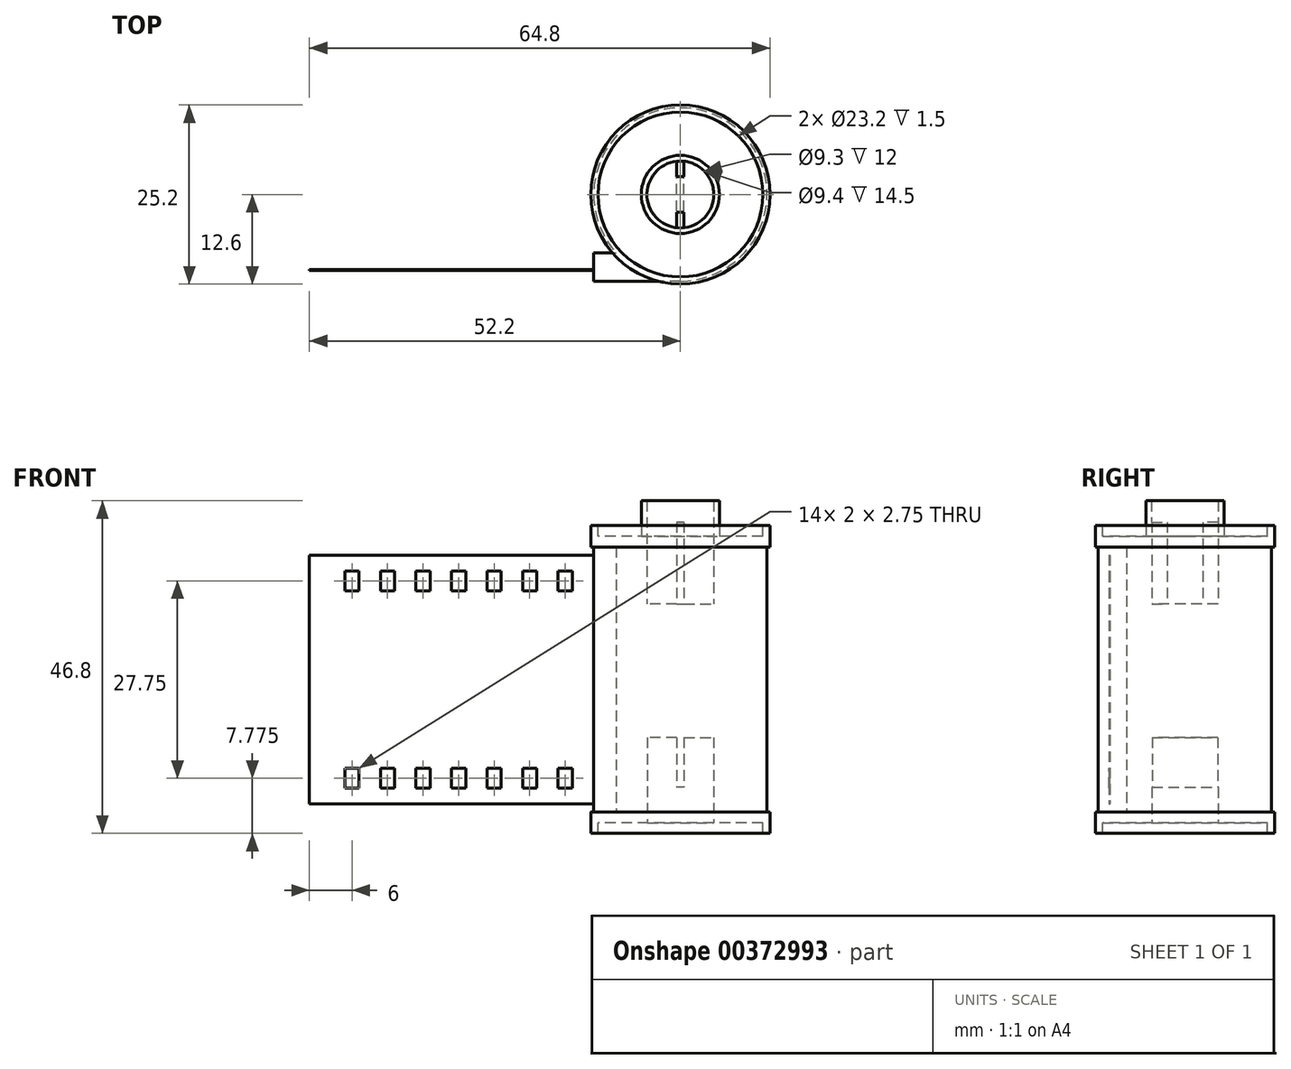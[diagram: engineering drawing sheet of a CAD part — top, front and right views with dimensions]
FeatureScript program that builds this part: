
annotation { "Feature Type Name" : "Feature", "Feature Type Description" : "" }
export const myFeature = defineFeature(function(context is Context, id is Id, definition is map)
    precondition{}
    {
        {
            var Q0;
            Q0=qCreatedBy(makeId("Top.planeOp"),FACE);
            var sketch = newSketch(context, id + "F0", { "sketchPlane" : qUnion([Q0])});
            skArc(sketch, "E0", {"start": v(0, -12.2) * mm, "mid": v(4.94, 11.16) * mm, "end": v(-9.03, -8.2) * mm});
            skLineSegment(sketch, "E1", {"start": v(0, -12.2) * mm, "end": v(-12.2, -12.2) * mm});
            skLineSegment(sketch, "E2", {"start": v(-12.2, -12.2) * mm, "end": v(-12.2, -8.2) * mm});
            skLineSegment(sketch, "E3", {"start": v(-12.2, -8.2) * mm, "end": v(-9.03, -8.2) * mm});
            skLineSegment(sketch, "E4", {"start": v(-12.2, -8.2) * mm, "end": v(-12.2, 0) * mm, "construction": true});
            skSolve(sketch);
        }
        {
            var Q0;
            Q0=makeQuery(id+"F0.imprint","IMPRINT",FACE,{"disambiguationData":[TD([[makeQuery(id+"F0.imprint","IMPRINT",EDGE,{"derivedFrom":sQuery(id+"F0.wireOp",EDGE,"E0")}),1.0]])]});
            extrude(context, id + "F1", {"entities" : qUnion([Q0]), "depth" : 37.3 * mm, "symmetric" : true});
        }
        {
            var Q0;
            Q0=qCreatedBy(makeId("Front.planeOp"),FACE);
            var sketch = newSketch(context, id + "F2", { "sketchPlane" : qUnion([Q0])});
            skLineSegment(sketch, "E5", {"start": v(0, -18.65) * mm, "end": v(12.6, -18.65) * mm});
            skLineSegment(sketch, "E6", {"start": v(12.6, -18.65) * mm, "end": v(12.6, -21.65) * mm});
            skLineSegment(sketch, "E7", {"start": v(11.6, -21.65) * mm, "end": v(11.6, -20.15) * mm});
            skLineSegment(sketch, "E8", {"start": v(11.6, -20.15) * mm, "end": v(0, -20.15) * mm});
            skLineSegment(sketch, "E9", {"start": v(11.6, -21.65) * mm, "end": v(12.6, -21.65) * mm});
            skLineSegment(sketch, "E10", {"start": v(0, -18.65) * mm, "end": v(0, -20.15) * mm});
            skSolve(sketch);
        }
        {
            var Q0;
            Q0=makeQuery(id+"F2.imprint","IMPRINT",FACE,{"disambiguationData":[TD([[makeQuery(id+"F2.imprint","IMPRINT",EDGE,{"derivedFrom":sQuery(id+"F2.wireOp",EDGE,"E5")}),-1.0]])]});
            var Q1;
            Q1=sQuery(id+"F2.wireOp",EDGE,"E10");
            revolve(context, id + "F3", {"operationType" : NewBodyOperationType.ADD, "entities" : qUnion([Q0]), "axis" : qUnion([Q1]), "revolveType" : RevolveType.FULL});
        }
        {
            var Q0;
            Q0=makeQuery(id+"F3.opRevolve","SWEPT_FACE",FACE,{"disambiguationData":[OSD([sQuery(id+"F2.wireOp",EDGE,"E8")])]});
            var sketch = newSketch(context, id + "F4", { "sketchPlane" : qUnion([Q0])});
            skCircle(sketch, "E11", {"center": v(0, 0) * mm, "radius": 4.65 * mm});
            skSolve(sketch);
        }
        {
            var Q0;
            Q0=makeQuery(id+"F4.imprint","IMPRINT",FACE,{"disambiguationData":[TD([[makeQuery(id+"F4.imprint","IMPRINT",EDGE,{"derivedFrom":sQuery(id+"F4.wireOp",EDGE,"E11")}),1.0]])]});
            extrude(context, id + "F5", {"entities" : qUnion([Q0]), "operationType" : NewBodyOperationType.REMOVE, "oppositeDirection" : true, "depth" : 5 * mm});
        }
        {
            var Q0;
            Q0=makeQuery(id+"F5.boolean.opBoolean","COPY",FACE,{"derivedFrom":makeQuery(id+"F5.opExtrude","CAP_FACE",FACE,{"disambiguationData":[OSD([sQuery(id+"F4.wireOp",EDGE,"E11")])],"isStart":false})});
            var sketch = newSketch(context, id + "F6", { "sketchPlane" : qUnion([Q0])});
            skArc(sketch, "E12", {"start": v(-0.5, 4.62) * mm, "mid": v(-4.65, 0) * mm, "end": v(-0.5, -4.62) * mm});
            skLineSegment(sketch, "E13", {"start": v(-0.5, 4.62) * mm, "end": v(-0.5, -4.62) * mm});
            skLineSegment(sketch, "E14", {"start": v(0, 0) * mm, "end": v(0, -10.24) * mm, "construction": true});
            skLineSegment(sketch, "E15.MirrorCS", {"start": v(0.5, 4.62) * mm, "end": v(0.5, -4.62) * mm});
            skArc(sketch, "E16.trimOffspring", {"start": v(0.5, -4.62) * mm, "mid": v(4.65, 0) * mm, "end": v(0.5, 4.62) * mm});
            skSolve(sketch);
        }
        {
            var Q0;
            Q0=makeQuery(id+"F6.imprint","IMPRINT",FACE,{"disambiguationData":[TD([[makeQuery(id+"F6.imprint","IMPRINT",EDGE,{"derivedFrom":sQuery(id+"F6.wireOp",EDGE,"E12")}),1.0]])]});
            var Q1;
            Q1=makeQuery(id+"F6.imprint","IMPRINT",FACE,{"disambiguationData":[TD([[makeQuery(id+"F6.imprint","IMPRINT",EDGE,{"derivedFrom":sQuery(id+"F6.wireOp",EDGE,"E15.MirrorCS")}),1.0]])]});
            extrude(context, id + "F7", {"entities" : qUnion([Q0, Q1]), "operationType" : NewBodyOperationType.REMOVE, "oppositeDirection" : true, "depth" : 7 * mm});
        }
        {
            var Q0;
            Q0=qCreatedBy(makeId("Front.planeOp"),FACE);
            var sketch = newSketch(context, id + "F8", { "sketchPlane" : qUnion([Q0])});
            skLineSegment(sketch, "E17", {"start": v(0, 18.65) * mm, "end": v(12.6, 18.65) * mm});
            skLineSegment(sketch, "E18", {"start": v(12.6, 18.65) * mm, "end": v(12.6, 21.65) * mm});
            skLineSegment(sketch, "E19", {"start": v(12.6, 21.65) * mm, "end": v(11.6, 21.65) * mm});
            skLineSegment(sketch, "E20", {"start": v(11.6, 21.65) * mm, "end": v(11.6, 20.15) * mm});
            skLineSegment(sketch, "E21", {"start": v(11.6, 20.15) * mm, "end": v(0, 20.15) * mm});
            skLineSegment(sketch, "E22", {"start": v(0, 20.15) * mm, "end": v(0, 18.65) * mm});
            skSolve(sketch);
        }
        {
            var Q0;
            Q0 = qSketchRegion(id + "F8", true);
            var Q1;
            Q1=sQuery(id+"F8.wireOp",EDGE,"E22");
            revolve(context, id + "F9", {"operationType" : NewBodyOperationType.ADD, "entities" : qUnion([Q0]), "axis" : qUnion([Q1]), "revolveType" : RevolveType.FULL});
        }
        {
            var Q0;
            Q0=makeQuery(id+"F9.opRevolve","SWEPT_FACE",FACE,{"disambiguationData":[OSD([sQuery(id+"F8.wireOp",EDGE,"E21")])]});
            var sketch = newSketch(context, id + "F10", { "sketchPlane" : qUnion([Q0])});
            skCircle(sketch, "E23", {"center": v(0, 0) * mm, "radius": 5.5 * mm});
            skCircle(sketch, "E24", {"center": v(0, 0) * mm, "radius": 4.7 * mm});
            skSolve(sketch);
        }
        {
            var Q0;
            Q0 = qSketchRegion(id + "F10", true);
            extrude(context, id + "F11", {"entities" : qUnion([Q0]), "operationType" : NewBodyOperationType.ADD, "depth" : 5 * mm});
        }
        {
            var Q0;
            Q0=makeQuery(id+"F11.boolean.opBoolean","SPLIT",FACE,{"disambiguationData":[TD([makeQuery(id+"F11.opExtrude","SWEPT_FACE",FACE,{"disambiguationData":[OSD([sQuery(id+"F10.wireOp",EDGE,"E24")])]})])],"derivedFrom":makeQuery(id+"F9.opRevolve","SWEPT_FACE",FACE,{"disambiguationData":[OSD([sQuery(id+"F8.wireOp",EDGE,"E21")])]})});
            var sketch = newSketch(context, id + "F12", { "sketchPlane" : qUnion([Q0])});
            skCircle(sketch, "E25.0", {"center": v(0, 0) * mm, "radius": 4.7 * mm});
            skSolve(sketch);
        }
        {
            var Q0;
            Q0=makeQuery(id+"F12.imprint","IMPRINT",FACE,{"disambiguationData":[TD([[makeQuery(id+"F12.imprint","IMPRINT",EDGE,{"derivedFrom":sQuery(id+"F12.wireOp",EDGE,"E25.0")}),1.0]])]});
            var Q1;
            Q1=sQuery(id+"F12.wireOp",EDGE,"E25.0");
            extrude(context, id + "F13", {"entities" : qUnion([Q0]), "operationType" : NewBodyOperationType.REMOVE, "surfaceEntities" : qUnion([Q1]), "oppositeDirection" : true, "depth" : 9.5 * mm});
        }
        {
            var Q0;
            Q0=makeQuery(id+"F13.boolean.opBoolean","COPY",FACE,{"derivedFrom":makeQuery(id+"F13.opExtrude","CAP_FACE",FACE,{"disambiguationData":[OSD([sQuery(id+"F12.wireOp",EDGE,"E25.0")])],"isStart":false})});
            var sketch = newSketch(context, id + "F14", { "sketchPlane" : qUnion([Q0])});
            skLineSegment(sketch, "E26", {"start": v(0, 0) * mm, "end": v(0, 19.86) * mm, "construction": true});
            skLineSegment(sketch, "E27", {"start": v(-0.5, 4.67) * mm, "end": v(-0.5, 2.5) * mm});
            skLineSegment(sketch, "E28.MirrorCS", {"start": v(0.5, 4.67) * mm, "end": v(0.5, 2.5) * mm});
            skLineSegment(sketch, "E29", {"start": v(-0.5, 2.5) * mm, "end": v(0.5, 2.5) * mm});
            skLineSegment(sketch, "E30", {"start": v(0, 0) * mm, "end": v(21.48, 0) * mm, "construction": true});
            skPoint(sketch, "E31.orphan", {"position": v(0.5, 8.35) * mm});
            skPoint(sketch, "E32.orphan", {"position": v(-0.5, 8.35) * mm});
            skLineSegment(sketch, "E33.MirrorCS", {"start": v(0.5, -4.67) * mm, "end": v(0.5, -2.5) * mm});
            skLineSegment(sketch, "E34.MirrorCS", {"start": v(-0.5, -2.5) * mm, "end": v(0.5, -2.5) * mm});
            skLineSegment(sketch, "E35.MirrorCS", {"start": v(-0.5, -4.67) * mm, "end": v(-0.5, -2.5) * mm});
            skArc(sketch, "E36.converted", {"start": v(-0.5, -4.67) * mm, "mid": v(3.14, -3.5) * mm, "end": v(4.7, 0) * mm});
            skArc(sketch, "E37.trimOffspring", {"start": v(0.5, 4.67) * mm, "mid": v(0, 4.7) * mm, "end": v(-0.5, 4.67) * mm});
            skSolve(sketch);
        }
        {
            var Q0;
            Q0 = qSketchRegion(id + "F14", true);
            extrude(context, id + "F15", {"entities" : qUnion([Q0]), "operationType" : NewBodyOperationType.ADD, "depth" : 11.5 * mm});
        }
        {
            var Q0;
            Q0=makeQuery(id+"F1.opExtrude","SWEPT_FACE",FACE,{"disambiguationData":[OSD([sQuery(id+"F0.wireOp",EDGE,"E1")])]});
            cPlane(context, id + "F16", {"entities" : qUnion([Q0]), "cplaneType" : CPlaneType.OFFSET, "offset" : 1.65 * mm, "oppositeDirection" : true, "width" : 150 * mm, "height" : 150 * mm});
        }
        {
            var Q0;
            Q0=qCreatedBy(id+"F16.planeOp",FACE);
            var sketch = newSketch(context, id + "F17", { "sketchPlane" : qUnion([Q0])});
            skLineSegment(sketch, "E38.bottom", {"start": v(-12.2, 17.5) * mm, "end": v(-52.2, 17.5) * mm});
            skLineSegment(sketch, "E38.top", {"start": v(-12.2, -17.5) * mm, "end": v(-52.2, -17.5) * mm});
            skLineSegment(sketch, "E38.left", {"start": v(-12.2, 17.5) * mm, "end": v(-12.2, -17.5) * mm});
            skLineSegment(sketch, "E38.right", {"start": v(-52.2, 17.5) * mm, "end": v(-52.2, -17.5) * mm});
            skLineSegment(sketch, "E39", {"start": v(-12.2, 0) * mm, "end": v(0, 0) * mm, "construction": true});
            skLineSegment(sketch, "E40.bottom", {"start": v(-15.2, 15.25) * mm, "end": v(-17.2, 15.25) * mm});
            skLineSegment(sketch, "E40.top", {"start": v(-15.2, 12.5) * mm, "end": v(-17.2, 12.5) * mm});
            skLineSegment(sketch, "E40.left", {"start": v(-15.2, 15.25) * mm, "end": v(-15.2, 12.5) * mm});
            skLineSegment(sketch, "E40.right", {"start": v(-17.2, 15.25) * mm, "end": v(-17.2, 12.5) * mm});
            skLineSegment(sketch, "E41.1.0.0", {"start": v(-20.2, 15.25) * mm, "end": v(-22.2, 15.25) * mm});
            skLineSegment(sketch, "E41.1.0.1", {"start": v(-20.2, 12.5) * mm, "end": v(-22.2, 12.5) * mm});
            skLineSegment(sketch, "E41.1.0.2", {"start": v(-20.2, 15.25) * mm, "end": v(-20.2, 12.5) * mm});
            skLineSegment(sketch, "E41.1.0.3", {"start": v(-22.2, 15.25) * mm, "end": v(-22.2, 12.5) * mm});
            skLineSegment(sketch, "E41.2.0.0", {"start": v(-25.2, 15.25) * mm, "end": v(-27.2, 15.25) * mm});
            skLineSegment(sketch, "E41.2.0.1", {"start": v(-25.2, 12.5) * mm, "end": v(-27.2, 12.5) * mm});
            skLineSegment(sketch, "E41.2.0.2", {"start": v(-25.2, 15.25) * mm, "end": v(-25.2, 12.5) * mm});
            skLineSegment(sketch, "E41.2.0.3", {"start": v(-27.2, 15.25) * mm, "end": v(-27.2, 12.5) * mm});
            skLineSegment(sketch, "E41.3.0.0", {"start": v(-30.2, 15.25) * mm, "end": v(-32.2, 15.25) * mm});
            skLineSegment(sketch, "E41.3.0.1", {"start": v(-30.2, 12.5) * mm, "end": v(-32.2, 12.5) * mm});
            skLineSegment(sketch, "E41.3.0.2", {"start": v(-30.2, 15.25) * mm, "end": v(-30.2, 12.5) * mm});
            skLineSegment(sketch, "E41.3.0.3", {"start": v(-32.2, 15.25) * mm, "end": v(-32.2, 12.5) * mm});
            skLineSegment(sketch, "E41.4.0.0", {"start": v(-35.2, 15.25) * mm, "end": v(-37.2, 15.25) * mm});
            skLineSegment(sketch, "E41.4.0.1", {"start": v(-35.2, 12.5) * mm, "end": v(-37.2, 12.5) * mm});
            skLineSegment(sketch, "E41.4.0.2", {"start": v(-35.2, 15.25) * mm, "end": v(-35.2, 12.5) * mm});
            skLineSegment(sketch, "E41.4.0.3", {"start": v(-37.2, 15.25) * mm, "end": v(-37.2, 12.5) * mm});
            skLineSegment(sketch, "E41.5.0.0", {"start": v(-40.2, 15.25) * mm, "end": v(-42.2, 15.25) * mm});
            skLineSegment(sketch, "E41.5.0.1", {"start": v(-40.2, 12.5) * mm, "end": v(-42.2, 12.5) * mm});
            skLineSegment(sketch, "E41.5.0.2", {"start": v(-40.2, 15.25) * mm, "end": v(-40.2, 12.5) * mm});
            skLineSegment(sketch, "E41.5.0.3", {"start": v(-42.2, 15.25) * mm, "end": v(-42.2, 12.5) * mm});
            skLineSegment(sketch, "E41.6.0.0", {"start": v(-45.2, 15.25) * mm, "end": v(-47.2, 15.25) * mm});
            skLineSegment(sketch, "E41.6.0.1", {"start": v(-45.2, 12.5) * mm, "end": v(-47.2, 12.5) * mm});
            skLineSegment(sketch, "E41.6.0.2", {"start": v(-45.2, 15.25) * mm, "end": v(-45.2, 12.5) * mm});
            skLineSegment(sketch, "E41.6.0.3", {"start": v(-47.2, 15.25) * mm, "end": v(-47.2, 12.5) * mm});
            skLineSegment(sketch, "E41.direction1", {"start": v(-17.2, 12.5) * mm, "end": v(-22.2, 12.5) * mm, "construction": true});
            skLineSegment(sketch, "E42.MirrorCS", {"start": v(-40.2, -15.25) * mm, "end": v(-42.2, -15.25) * mm});
            skLineSegment(sketch, "E43.MirrorCS", {"start": v(-30.2, -12.5) * mm, "end": v(-32.2, -12.5) * mm});
            skLineSegment(sketch, "E44.MirrorCS", {"start": v(-45.2, -12.5) * mm, "end": v(-47.2, -12.5) * mm});
            skLineSegment(sketch, "E45.MirrorCS", {"start": v(-35.2, -15.25) * mm, "end": v(-37.2, -15.25) * mm});
            skLineSegment(sketch, "E46.MirrorCS", {"start": v(-30.2, -15.25) * mm, "end": v(-32.2, -15.25) * mm});
            skLineSegment(sketch, "E47.MirrorCS", {"start": v(-25.2, -12.5) * mm, "end": v(-27.2, -12.5) * mm});
            skLineSegment(sketch, "E48.MirrorCS", {"start": v(-45.2, -15.25) * mm, "end": v(-47.2, -15.25) * mm});
            skLineSegment(sketch, "E49.MirrorCS", {"start": v(-20.2, -12.5) * mm, "end": v(-22.2, -12.5) * mm});
            skLineSegment(sketch, "E50.MirrorCS", {"start": v(-20.2, -15.25) * mm, "end": v(-22.2, -15.25) * mm});
            skLineSegment(sketch, "E51.MirrorCS", {"start": v(-15.2, -12.5) * mm, "end": v(-17.2, -12.5) * mm});
            skLineSegment(sketch, "E52.MirrorCS", {"start": v(-15.2, -15.25) * mm, "end": v(-17.2, -15.25) * mm});
            skLineSegment(sketch, "E53.MirrorCS", {"start": v(-40.2, -12.5) * mm, "end": v(-42.2, -12.5) * mm});
            skLineSegment(sketch, "E54.MirrorCS", {"start": v(-25.2, -15.25) * mm, "end": v(-27.2, -15.25) * mm});
            skLineSegment(sketch, "E55.MirrorCS", {"start": v(-35.2, -12.5) * mm, "end": v(-37.2, -12.5) * mm});
            skLineSegment(sketch, "E56.MirrorCS", {"start": v(-47.2, -15.25) * mm, "end": v(-47.2, -12.5) * mm});
            skLineSegment(sketch, "E57.MirrorCS", {"start": v(-27.2, -15.25) * mm, "end": v(-27.2, -12.5) * mm});
            skLineSegment(sketch, "E58.MirrorCS", {"start": v(-30.2, -15.25) * mm, "end": v(-30.2, -12.5) * mm});
            skLineSegment(sketch, "E59.MirrorCS", {"start": v(-40.2, -15.25) * mm, "end": v(-40.2, -12.5) * mm});
            skLineSegment(sketch, "E60.MirrorCS", {"start": v(-35.2, -15.25) * mm, "end": v(-35.2, -12.5) * mm});
            skLineSegment(sketch, "E61.MirrorCS", {"start": v(-37.2, -15.25) * mm, "end": v(-37.2, -12.5) * mm});
            skLineSegment(sketch, "E62.MirrorCS", {"start": v(-17.2, -12.5) * mm, "end": v(-22.2, -12.5) * mm, "construction": true});
            skLineSegment(sketch, "E63.MirrorCS", {"start": v(-42.2, -15.25) * mm, "end": v(-42.2, -12.5) * mm});
            skLineSegment(sketch, "E64.MirrorCS", {"start": v(-25.2, -15.25) * mm, "end": v(-25.2, -12.5) * mm});
            skLineSegment(sketch, "E65.MirrorCS", {"start": v(-22.2, -15.25) * mm, "end": v(-22.2, -12.5) * mm});
            skLineSegment(sketch, "E66.MirrorCS", {"start": v(-20.2, -15.25) * mm, "end": v(-20.2, -12.5) * mm});
            skLineSegment(sketch, "E67.MirrorCS", {"start": v(-32.2, -15.25) * mm, "end": v(-32.2, -12.5) * mm});
            skLineSegment(sketch, "E68.MirrorCS", {"start": v(-17.2, -15.25) * mm, "end": v(-17.2, -12.5) * mm});
            skLineSegment(sketch, "E69.MirrorCS", {"start": v(-15.2, -15.25) * mm, "end": v(-15.2, -12.5) * mm});
            skLineSegment(sketch, "E70.MirrorCS", {"start": v(-45.2, -15.25) * mm, "end": v(-45.2, -12.5) * mm});
            skSolve(sketch);
        }
        {
            var Q0;
            Q0 = qSketchRegion(id + "F17", true);
            extrude(context, id + "F18", {"entities" : qUnion([Q0]), "operationType" : NewBodyOperationType.ADD, "depth" : 0.14 * mm});
        }
    });
